annotation { "Feature Type Name" : "Feature", "Feature Type Description" : "" }
export const myFeature = defineFeature(function(context is Context, id is Id, definition is map)
    precondition{}
    {
        {
            var Q0;
            Q0=qCreatedBy(makeId("Top.planeOp"),FACE);
            var sketch = newSketch(context, id + "F0", { "sketchPlane" : qUnion([Q0])});
            skLineSegment(sketch, "E0", {"start": v(5.96, -71.34) * mm, "end": v(49.08, -1.48) * mm});
            skArc(sketch, "E1", {"start": v(50.45, 2.18) * mm, "mid": v(32.75, 30.86) * mm, "end": v(1.8, 17.51) * mm});
            skLineSegment(sketch, "E2.MirrorCS", {"start": v(-5.96, -71.34) * mm, "end": v(-49.08, -1.48) * mm});
            skArc(sketch, "E3.MirrorCS", {"start": v(-50.45, 2.18) * mm, "mid": v(-32.75, 30.86) * mm, "end": v(-1.8, 17.51) * mm});
            skPoint(sketch, "E4.orphan", {"position": v(0, 0) * mm});
            skPoint(sketch, "E5.visualSharp", {"position": v(0, -80.98) * mm});
            skArc(sketch, "E5.filletArc", {"start": v(-5.96, -71.34) * mm, "mid": v(0, -74.66) * mm, "end": v(5.96, -71.34) * mm});
            skPoint(sketch, "E6.visualSharp", {"position": v(50, 0) * mm});
            skArc(sketch, "E6.filletArc", {"start": v(49.08, -1.48) * mm, "mid": v(49.95, 0.28) * mm, "end": v(50.45, 2.18) * mm});
            skPoint(sketch, "E7.visualSharp", {"position": v(-50, 0) * mm});
            skArc(sketch, "E7.filletArc", {"start": v(-50.45, 2.18) * mm, "mid": v(-49.95, 0.28) * mm, "end": v(-49.08, -1.48) * mm});
            skPoint(sketch, "E8.visualSharp", {"position": v(0, 12.56) * mm});
            skArc(sketch, "E8.filletArc", {"start": v(-1.8, 17.51) * mm, "mid": v(0, 16.39) * mm, "end": v(1.8, 17.51) * mm});
            skSolve(sketch);
        }
        {
            var Q0;
            Q0 = qSketchRegion(id + "F0", true);
            extrude(context, id + "F1", {"entities" : qUnion([Q0]), "depth" : 15 * mm, "offsetDistance" : 25 * mm});
        }
        {
            var Q0;
            Q0=makeQuery(id+"F1.opExtrude","CAP_FACE",FACE,{"disambiguationData":[OSD([sQuery(id+"F0.wireOp",EDGE,"E0"),sQuery(id+"F0.wireOp",EDGE,"E1"),sQuery(id+"F0.wireOp",EDGE,"E2.MirrorCS"),sQuery(id+"F0.wireOp",EDGE,"E3.MirrorCS"),sQuery(id+"F0.wireOp",EDGE,"E5.filletArc"),sQuery(id+"F0.wireOp",EDGE,"E6.filletArc"),sQuery(id+"F0.wireOp",EDGE,"E7.filletArc"),sQuery(id+"F0.wireOp",EDGE,"E8.filletArc")])],"isStart":false});
            var sketch = newSketch(context, id + "F2", { "sketchPlane" : qUnion([Q0])});
            skLineSegment(sketch, "E9.bottom", {"start": v(-45.05, -3.25) * mm, "end": v(44.95, -3.25) * mm});
            skLineSegment(sketch, "E9.top", {"start": v(-45.05, 9.75) * mm, "end": v(44.95, 9.75) * mm});
            skLineSegment(sketch, "E9.left", {"start": v(-45.05, -3.25) * mm, "end": v(-45.05, 9.75) * mm});
            skLineSegment(sketch, "E9.right", {"start": v(44.95, -3.25) * mm, "end": v(44.95, 9.75) * mm});
            skCircle(sketch, "E10", {"center": v(-36, 19.17) * mm, "radius": 5 * mm});
            skCircle(sketch, "E11", {"center": v(-14, 19.17) * mm, "radius": 5 * mm});
            skCircle(sketch, "E12", {"center": v(14, 19.17) * mm, "radius": 5 * mm});
            skCircle(sketch, "E13", {"center": v(36, 19.17) * mm, "radius": 5 * mm});
            skLineSegment(sketch, "E14", {"start": v(-25, 6.28) * mm, "end": v(-25, 32.06) * mm, "construction": true});
            skLineSegment(sketch, "E15", {"start": v(-47.32, 19.17) * mm, "end": v(-2.68, 19.17) * mm, "construction": true});
            skPoint(sketch, "E15.startSnap0", {"position": v(-25, 19.17) * mm});
            skLineSegment(sketch, "E16", {"start": v(25, 6.28) * mm, "end": v(25, 32.06) * mm, "construction": true});
            skLineSegment(sketch, "E17", {"start": v(47.32, 19.17) * mm, "end": v(2.68, 19.17) * mm, "construction": true});
            skPoint(sketch, "E17.startSnap0", {"position": v(25, 19.17) * mm});
            skLineSegment(sketch, "E18.0", {"start": v(1.87, -68.81) * mm, "end": v(23.96, -33.05) * mm});
            skArc(sketch, "E18.1", {"start": v(-1.87, -68.81) * mm, "mid": v(0, -69.86) * mm, "end": v(1.87, -68.81) * mm});
            skLineSegment(sketch, "E18.2", {"start": v(-1.87, -68.81) * mm, "end": v(-23.96, -33.05) * mm});
            skLineSegment(sketch, "E19", {"start": v(-22.25, -30) * mm, "end": v(22.25, -30) * mm});
            skPoint(sketch, "E20.visualSharp", {"position": v(-25.84, -30) * mm});
            skArc(sketch, "E20.filletArc", {"start": v(-22.25, -30) * mm, "mid": v(-24, -31.02) * mm, "end": v(-23.96, -33.05) * mm});
            skPoint(sketch, "E21.visualSharp", {"position": v(25.84, -30) * mm});
            skArc(sketch, "E21.filletArc", {"start": v(23.96, -33.05) * mm, "mid": v(24, -31.02) * mm, "end": v(22.25, -30) * mm});
            skSolve(sketch);
        }
        {
            var Q0;
            Q0 = qSketchRegion(id + "F2", true);
            extrude(context, id + "F3", {"entities" : qUnion([Q0]), "operationType" : NewBodyOperationType.REMOVE, "oppositeDirection" : true, "depth" : 12 * mm, "offsetDistance" : 25 * mm});
        }
        {
            var Q0;
            Q0=makeQuery(id+"F1.opExtrude","CAP_FACE",FACE,{"disambiguationData":[OSD([sQuery(id+"F0.wireOp",EDGE,"E0"),sQuery(id+"F0.wireOp",EDGE,"E1"),sQuery(id+"F0.wireOp",EDGE,"E2.MirrorCS"),sQuery(id+"F0.wireOp",EDGE,"E3.MirrorCS"),sQuery(id+"F0.wireOp",EDGE,"E5.filletArc"),sQuery(id+"F0.wireOp",EDGE,"E6.filletArc"),sQuery(id+"F0.wireOp",EDGE,"E7.filletArc"),sQuery(id+"F0.wireOp",EDGE,"E8.filletArc")])],"isStart":true});
            var sketch = newSketch(context, id + "F4", { "sketchPlane" : qUnion([Q0])});
            skArc(sketch, "E22.0", {"start": v(-51.98, 3.27) * mm, "mid": v(-53.13, 0.9) * mm, "end": v(-53.8, -1.64) * mm});
            skLineSegment(sketch, "E22.1", {"start": v(-8.85, 73.12) * mm, "end": v(-51.98, 3.27) * mm});
            skArc(sketch, "E22.2", {"start": v(0, -21.32) * mm, "mid": v(35.02, -33.68) * mm, "end": v(53.8, -1.64) * mm});
            skArc(sketch, "E22.3", {"start": v(53.8, -1.64) * mm, "mid": v(53.13, 0.9) * mm, "end": v(51.98, 3.27) * mm});
            skLineSegment(sketch, "E22.4", {"start": v(51.98, 3.27) * mm, "end": v(8.85, 73.12) * mm});
            skArc(sketch, "E22.5", {"start": v(-53.8, -1.64) * mm, "mid": v(-35.02, -33.68) * mm, "end": v(0, -21.32) * mm});
            skArc(sketch, "E22.6", {"start": v(8.85, 73.12) * mm, "mid": v(0, 78.06) * mm, "end": v(-8.85, 73.12) * mm});
            skSolve(sketch);
        }
        {
            var Q0;
            Q0 = qSketchRegion(id + "F4", true);
            extrude(context, id + "F5", {"entities" : qUnion([Q0]), "operationType" : NewBodyOperationType.ADD, "depth" : 2 * mm, "offsetDistance" : 25 * mm});
        }
        {
            var Q0;
            Q0=makeQuery(id+"F3.boolean.opBoolean","COPY",FACE,{"derivedFrom":makeQuery(id+"F3.opExtrude","CAP_FACE",FACE,{"disambiguationData":[OSD([sQuery(id+"F2.wireOp",EDGE,"E10")])],"isStart":false})});
            var sketch = newSketch(context, id + "F6", { "sketchPlane" : qUnion([Q0])});
            skCircle(sketch, "E23.0.0", {"center": v(-14, 19.17) * mm, "radius": 5 * mm});
            skCircle(sketch, "E24.0.0", {"center": v(14, 19.17) * mm, "radius": 5 * mm});
            skCircle(sketch, "E25.0.0", {"center": v(36, 19.17) * mm, "radius": 5 * mm});
            skCircle(sketch, "E26.0.0", {"center": v(-36, 19.17) * mm, "radius": 5 * mm});
            skCircle(sketch, "E27.0", {"center": v(-36, 19.17) * mm, "radius": 4 * mm});
            skCircle(sketch, "E28.0", {"center": v(-14, 19.17) * mm, "radius": 4 * mm});
            skCircle(sketch, "E29.0", {"center": v(14, 19.17) * mm, "radius": 4 * mm});
            skCircle(sketch, "E30.0", {"center": v(36, 19.17) * mm, "radius": 4 * mm});
            skSolve(sketch);
        }
        {
            var Q0;
            Q0 = qSketchRegion(id + "F6", true);
            extrude(context, id + "F7", {"entities" : qUnion([Q0]), "operationType" : NewBodyOperationType.ADD, "depth" : 25 * mm, "offsetDistance" : 25 * mm});
        }
        {
            var Q0;
            Q0=makeQuery(id+"F1.opExtrude","CAP_FACE",FACE,{"disambiguationData":[OSD([sQuery(id+"F0.wireOp",EDGE,"E0"),sQuery(id+"F0.wireOp",EDGE,"E1"),sQuery(id+"F0.wireOp",EDGE,"E2.MirrorCS"),sQuery(id+"F0.wireOp",EDGE,"E3.MirrorCS"),sQuery(id+"F0.wireOp",EDGE,"E5.filletArc"),sQuery(id+"F0.wireOp",EDGE,"E6.filletArc"),sQuery(id+"F0.wireOp",EDGE,"E7.filletArc"),sQuery(id+"F0.wireOp",EDGE,"E8.filletArc")])],"isStart":false});
            var sketch = newSketch(context, id + "F8", { "sketchPlane" : qUnion([Q0])});
            skText(sketch, "E31", { "text": "Executive Director", "fontName": "OpenSans-Bold.ttf"});
            skLineSegment(sketch, "E32", {"start": v(-40.98, -5.75) * mm, "end": v(-40.98, -3.25) * mm, "construction": true});
            skLineSegment(sketch, "E33", {"start": v(40.88, -5.75) * mm, "end": v(40.88, -3.25) * mm, "construction": true});
            skText(sketch, "E34", { "text": "Judi Stapley", "fontName": "OpenSans-Bold.ttf"});
            skLineSegment(sketch, "E35", {"start": v(-31.78, -15.15) * mm, "end": v(-31.78, -12.15) * mm, "construction": true});
            skLineSegment(sketch, "E36", {"start": v(36.88, -15.15) * mm, "end": v(36.88, -12.15) * mm, "construction": true});
            const initialGuessF8  = {"E31": [-0.04046, -0.012, 1, 0, 0.00625], "E34": [-0.03126, -0.023, 1, 0, 0.008]};
            skSetInitialGuess(sketch, initialGuessF8);
            skSolve(sketch);
        }
        {
            var Q0;
            Q0 = qSketchRegion(id + "F8", true);
            extrude(context, id + "F9", {"entities" : qUnion([Q0]), "operationType" : NewBodyOperationType.REMOVE, "oppositeDirection" : true, "depth" : 1.5 * mm, "offsetDistance" : 25 * mm});
        }
        {
            var Q0;
            Q0=makeQuery(id+"F1.opExtrude","CAP_EDGE",EDGE,{"disambiguationData":[OSD([sQuery(id+"F0.wireOp",EDGE,"E1")])],"isStart":false});
            var Q1;
            Q1=makeQuery(id+"F1.opExtrude","CAP_EDGE",EDGE,{"disambiguationData":[OSD([sQuery(id+"F0.wireOp",EDGE,"E6.filletArc")])],"isStart":false});
            var Q2;
            Q2=makeQuery(id+"F1.opExtrude","CAP_EDGE",EDGE,{"disambiguationData":[OSD([sQuery(id+"F0.wireOp",EDGE,"E0")])],"isStart":false});
            var Q3;
            Q3=makeQuery(id+"F1.opExtrude","CAP_EDGE",EDGE,{"disambiguationData":[OSD([sQuery(id+"F0.wireOp",EDGE,"E5.filletArc")])],"isStart":false});
            var Q4;
            Q4=makeQuery(id+"F1.opExtrude","CAP_EDGE",EDGE,{"disambiguationData":[OSD([sQuery(id+"F0.wireOp",EDGE,"E2.MirrorCS")])],"isStart":false});
            var Q5;
            Q5=makeQuery(id+"F1.opExtrude","CAP_EDGE",EDGE,{"disambiguationData":[OSD([sQuery(id+"F0.wireOp",EDGE,"E3.MirrorCS")])],"isStart":false});
            var Q6;
            Q6=makeQuery(id+"F1.opExtrude","CAP_EDGE",EDGE,{"disambiguationData":[OSD([sQuery(id+"F0.wireOp",EDGE,"E7.filletArc")])],"isStart":false});
            var Q7;
            Q7=makeQuery(id+"F1.opExtrude","CAP_EDGE",EDGE,{"disambiguationData":[OSD([sQuery(id+"F0.wireOp",EDGE,"E8.filletArc")])],"isStart":false});
            fillet(context, id + "F10", {"entities" : qUnion([Q0, Q1, Q2, Q3, Q4, Q5, Q6, Q7]), "radius" : 1 * mm, "tangentPropagation" : true, "allowEdgeOverflow" : false});
        }
        {
            var Q0;
            Q0=makeQuery(id+"F7.opExtrude","CAP_EDGE",EDGE,{"disambiguationData":[OSD([sQuery(id+"F6.wireOp",EDGE,"E27.0")])],"isStart":false});
            var Q1;
            Q1=makeQuery(id+"F7.opExtrude","CAP_EDGE",EDGE,{"disambiguationData":[OSD([sQuery(id+"F6.wireOp",EDGE,"E28.0")])],"isStart":false});
            var Q2;
            Q2=makeQuery(id+"F7.opExtrude","CAP_EDGE",EDGE,{"disambiguationData":[OSD([sQuery(id+"F6.wireOp",EDGE,"E29.0")])],"isStart":false});
            var Q3;
            Q3=makeQuery(id+"F7.opExtrude","CAP_EDGE",EDGE,{"disambiguationData":[OSD([sQuery(id+"F6.wireOp",EDGE,"E30.0")])],"isStart":false});
            fillet(context, id + "F11", {"entities" : qUnion([Q0, Q1, Q2, Q3]), "radius" : 5 * mm, "tangentPropagation" : true, "allowEdgeOverflow" : false});
        }
    });